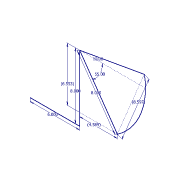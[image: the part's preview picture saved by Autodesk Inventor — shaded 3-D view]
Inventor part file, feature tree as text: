
AUTODESK INVENTOR PART (.ipt)
format: ipt  version: 2012 (Build 160160000, 160)  size: 65,024 bytes
history: native  units: in
note: dims shown in document units (in); Inventor stores cm internally (conversion verified against a paired STEP export)
features: sketch x1
ambient origin geometry x8: Origin, YZ Plane, XZ Plane, XY Plane, X Axis, Y Axis, Z Axis, Center Point
feature tree (1):
  sketch  "Sketch1"  dims[d1=0.3779in d2=0.0687in d3=8.0in d4=8.5968in d5=8.0in d6=6.0in d7=6.5532in d8=4.5886in]
